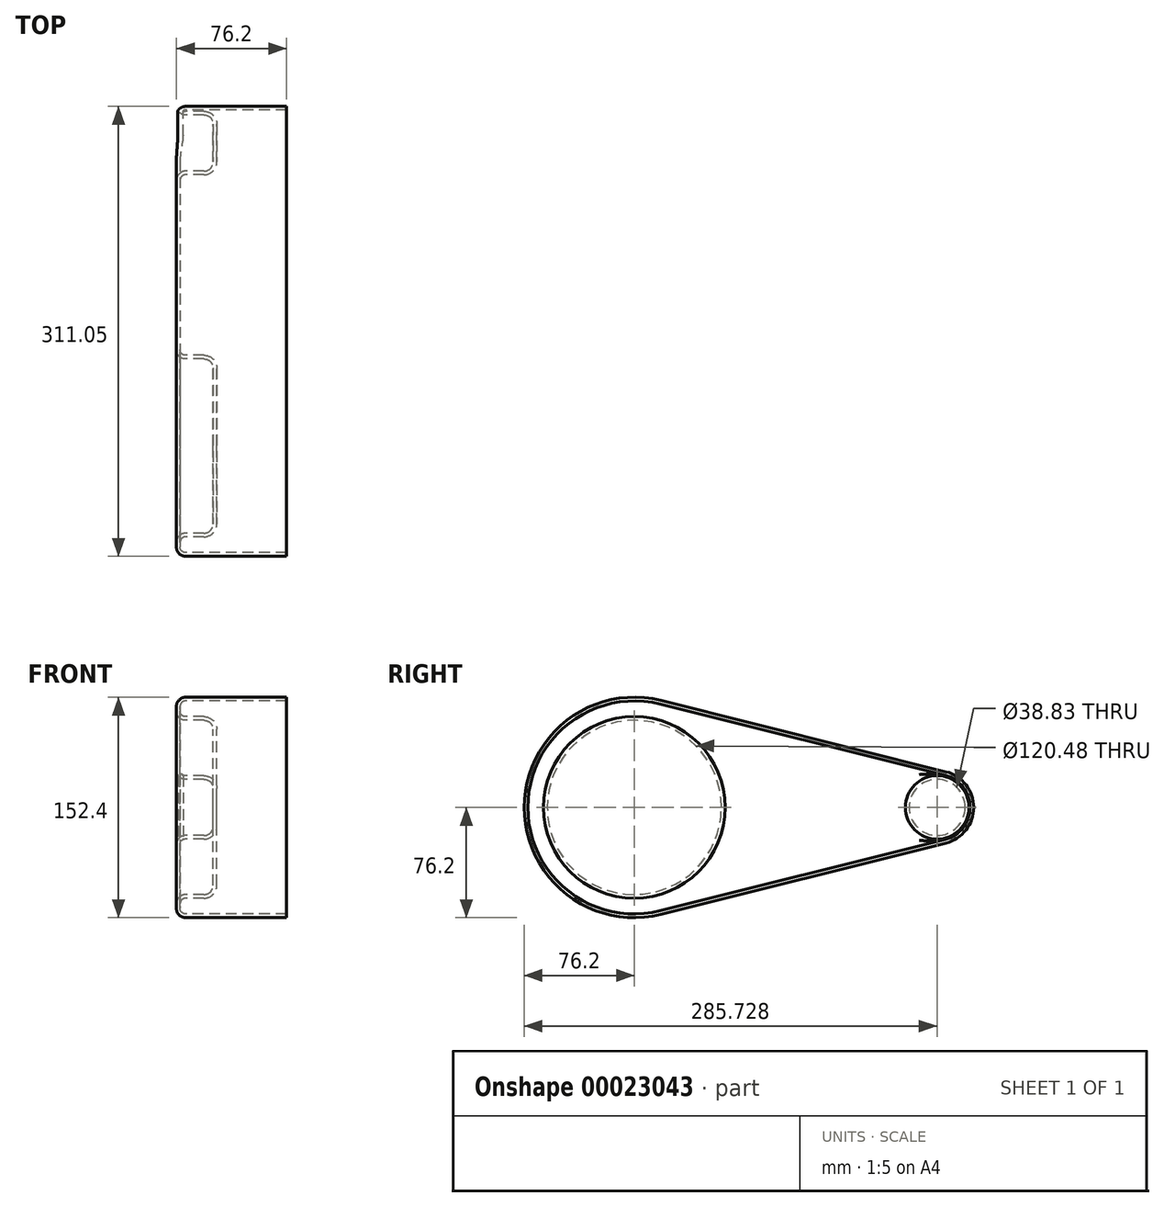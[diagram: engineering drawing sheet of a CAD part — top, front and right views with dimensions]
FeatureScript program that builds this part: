
annotation { "Feature Type Name" : "Feature", "Feature Type Description" : "" }
export const myFeature = defineFeature(function(context is Context, id is Id, definition is map)
    precondition{}
    {
        {
            var Q0;
            Q0=qCreatedBy(makeId("Right.planeOp"),FACE);
            var sketch = newSketch(context, id + "F0", { "sketchPlane" : qUnion([Q0])});
            skCircle(sketch, "E0", {"center": v(0, 0) * mm, "radius": 76.2 * mm});
            skCircle(sketch, "E1", {"center": v(209.45, 0) * mm, "radius": 25.4 * mm});
            skLineSegment(sketch, "E2", {"start": v(18.48, 73.92) * mm, "end": v(215.61, 24.64) * mm});
            skLineSegment(sketch, "E3", {"start": v(18.48, -73.92) * mm, "end": v(215.61, -24.64) * mm});
            skSolve(sketch);
        }
        {
            var Q0;
            {var subQ0=sQuery(id+"F0.wireOp",EDGE,"E0");var subQ2=makeQuery(id+"F0.imprint","INTERSECT",VERTEX,{"derivedFrom":[subQ0,sQuery(id+"F0.wireOp",EDGE,"E2")]});Q0=makeQuery(id+"F0.imprint","IMPRINT",FACE,{"disambiguationData":[TD([[makeQuery(id+"F0.imprint","IMPRINT",EDGE,{"disambiguationData":[TD([[subQ2,-1.0]])],"derivedFrom":subQ0}),1.0]])]});}
            var Q1;
            {var subQ1=sQuery(id+"F0.wireOp",EDGE,"E2");Q1=makeQuery(id+"F0.imprint","IMPRINT",FACE,{"disambiguationData":[TD([[makeQuery(id+"F0.imprint","IMPRINT",EDGE,{"derivedFrom":subQ1}),-1.0]])]});}
            var Q2;
            {var subQ0=sQuery(id+"F0.wireOp",EDGE,"E1");var subQ2=makeQuery(id+"F0.imprint","INTERSECT",VERTEX,{"derivedFrom":[subQ0,sQuery(id+"F0.wireOp",EDGE,"E2")]});Q2=makeQuery(id+"F0.imprint","IMPRINT",FACE,{"disambiguationData":[TD([[makeQuery(id+"F0.imprint","IMPRINT",EDGE,{"disambiguationData":[TD([[subQ2,-1.0]])],"derivedFrom":subQ0}),1.0]])]});}
            extrude(context, id + "F1", {"entities" : qUnion([Q0, Q1, Q2]), "depth" : 76.2 * mm});
        }
        {
            var Q0;
            Q0=qCreatedBy(makeId("Right.planeOp"),FACE);
            var sketch = newSketch(context, id + "F2", { "sketchPlane" : qUnion([Q0])});
            skCircle(sketch, "E4", {"center": v(0, 0) * mm, "radius": 60.24 * mm});
            skCircle(sketch, "E5", {"center": v(209.53, 0) * mm, "radius": 19.41 * mm});
            skSolve(sketch);
        }
        {
            var Q0;
            Q0 = qSketchRegion(id + "F2", true);
            extrude(context, id + "F3", {"entities" : qUnion([Q0]), "operationType" : NewBodyOperationType.REMOVE, "depth" : 25.4 * mm});
        }
        {
            var Q0;
            Q0=makeQuery(id+"F1.opExtrude","CAP_FACE",FACE,{"disambiguationData":[OSD([sQuery(id+"F0.wireOp",EDGE,"E0"),sQuery(id+"F0.wireOp",EDGE,"E1"),sQuery(id+"F0.wireOp",EDGE,"E2"),sQuery(id+"F0.wireOp",EDGE,"E3")])],"isStart":true});
            var Q1;
            Q1=makeQuery(id+"F3.boolean.opBoolean","COPY",FACE,{"derivedFrom":makeQuery(id+"F3.opExtrude","CAP_FACE",FACE,{"disambiguationData":[OSD([sQuery(id+"F2.wireOp",EDGE,"E5")])],"isStart":false})});
            var Q2;
            Q2=makeQuery(id+"F3.boolean.opBoolean","COPY",FACE,{"derivedFrom":makeQuery(id+"F3.opExtrude","CAP_FACE",FACE,{"disambiguationData":[OSD([sQuery(id+"F2.wireOp",EDGE,"E4")])],"isStart":false})});
            fillet(context, id + "F4", {"entities" : qUnion([Q0, Q1, Q2]), "radius" : 6.35 * mm, "tangentPropagation" : true, "allowEdgeOverflow" : false});
        }
        {
            var Q0;
            Q0=makeQuery(id+"F1.opExtrude","CAP_FACE",FACE,{"disambiguationData":[OSD([sQuery(id+"F0.wireOp",EDGE,"E0"),sQuery(id+"F0.wireOp",EDGE,"E1"),sQuery(id+"F0.wireOp",EDGE,"E2"),sQuery(id+"F0.wireOp",EDGE,"E3")])],"isStart":false});
            shell(context, id + "F5", {"entities" : qUnion([Q0]), "thickness" : 2.54 * mm});
        }
    });
